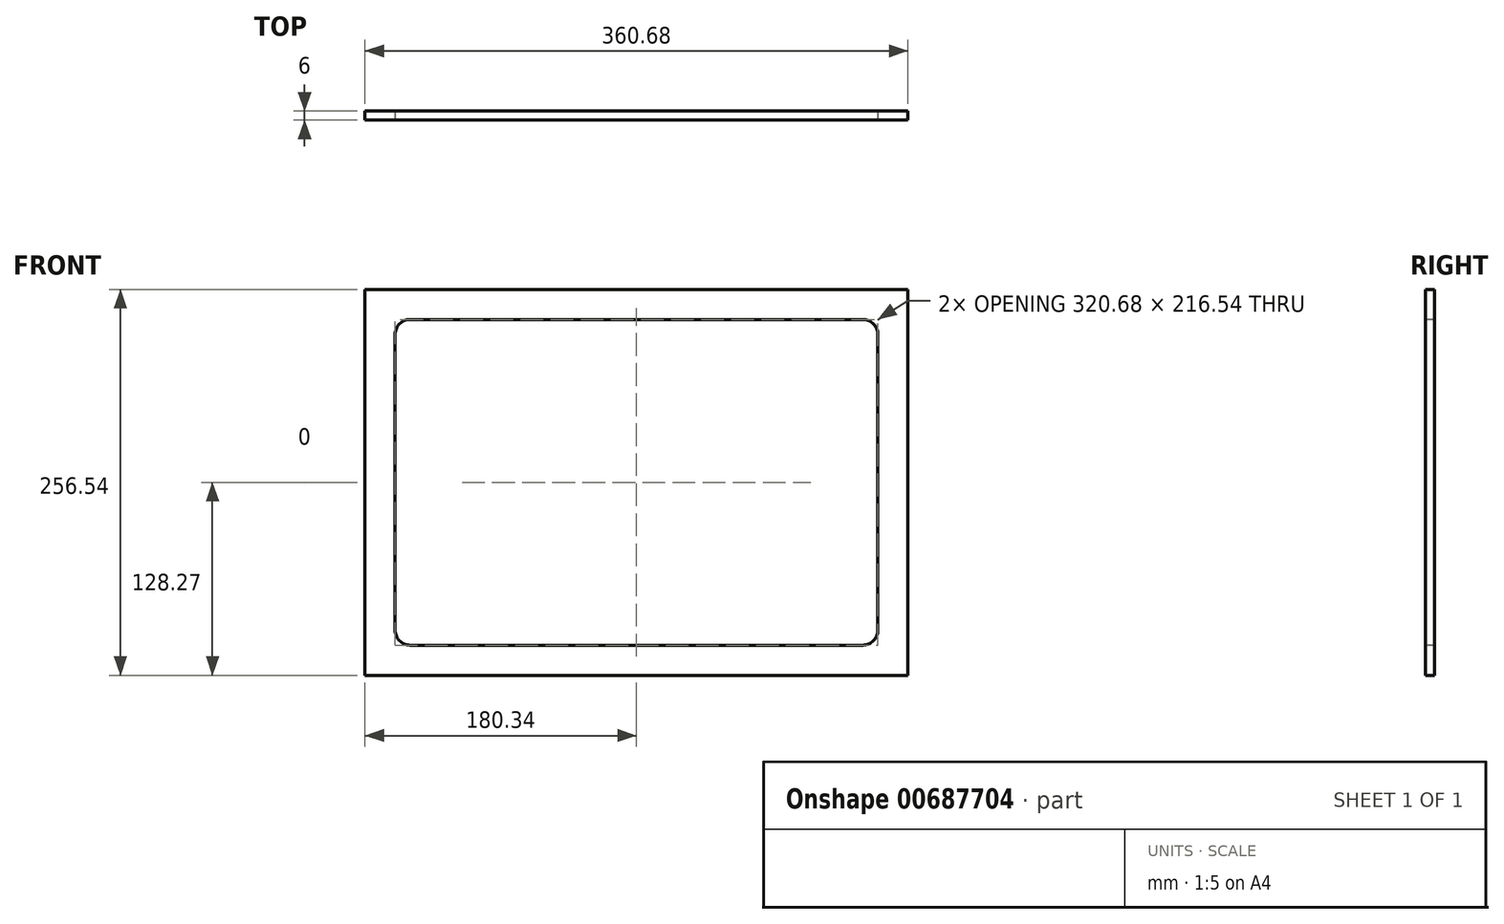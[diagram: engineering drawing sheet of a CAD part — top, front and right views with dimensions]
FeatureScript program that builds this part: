
annotation { "Feature Type Name" : "Feature", "Feature Type Description" : "" }
export const myFeature = defineFeature(function(context is Context, id is Id, definition is map)
    precondition{}
    {
        {
            var Q0;
            Q0=qCreatedBy(makeId("Front.planeOp"),FACE);
            var sketch = newSketch(context, id + "F0", { "sketchPlane" : qUnion([Q0])});
            skLineSegment(sketch, "E0.bottom", {"start": v(-180.34, 128.27) * mm, "end": v(180.34, 128.27) * mm});
            skLineSegment(sketch, "E0.top", {"start": v(-180.34, -128.27) * mm, "end": v(180.34, -128.27) * mm});
            skLineSegment(sketch, "E0.left", {"start": v(-180.34, 128.27) * mm, "end": v(-180.34, -128.27) * mm});
            skLineSegment(sketch, "E0.right", {"start": v(180.34, 128.27) * mm, "end": v(180.34, -128.27) * mm});
            skLineSegment(sketch, "E1", {"start": v(0, 0) * mm, "end": v(0, 128.27) * mm, "construction": true});
            skLineSegment(sketch, "E2", {"start": v(0, 0) * mm, "end": v(0, -128.27) * mm, "construction": true});
            skLineSegment(sketch, "E3", {"start": v(0, 0) * mm, "end": v(-180.34, 0) * mm, "construction": true});
            skLineSegment(sketch, "E4", {"start": v(0, 0) * mm, "end": v(180.34, 0) * mm, "construction": true});
            skLineSegment(sketch, "E5.0", {"start": v(-150.34, 108.27) * mm, "end": v(150.34, 108.27) * mm});
            skLineSegment(sketch, "E5.1", {"start": v(-160.34, 98.27) * mm, "end": v(-160.34, -98.27) * mm});
            skLineSegment(sketch, "E5.2", {"start": v(-150.34, -108.27) * mm, "end": v(150.34, -108.27) * mm});
            skLineSegment(sketch, "E5.3", {"start": v(160.34, 98.27) * mm, "end": v(160.34, -98.27) * mm});
            skPoint(sketch, "E6.visualSharp", {"position": v(-160.34, 108.27) * mm});
            skArc(sketch, "E6.filletArc", {"start": v(-150.34, 108.27) * mm, "mid": v(-157.41, 105.34) * mm, "end": v(-160.34, 98.27) * mm});
            skPoint(sketch, "E7.visualSharp", {"position": v(160.34, 108.27) * mm});
            skArc(sketch, "E7.filletArc", {"start": v(160.34, 98.27) * mm, "mid": v(157.41, 105.34) * mm, "end": v(150.34, 108.27) * mm});
            skPoint(sketch, "E8.visualSharp", {"position": v(160.34, -108.27) * mm});
            skArc(sketch, "E8.filletArc", {"start": v(150.34, -108.27) * mm, "mid": v(157.41, -105.34) * mm, "end": v(160.34, -98.27) * mm});
            skPoint(sketch, "E9.visualSharp", {"position": v(-160.34, -108.27) * mm});
            skArc(sketch, "E9.filletArc", {"start": v(-160.34, -98.27) * mm, "mid": v(-157.41, -105.34) * mm, "end": v(-150.34, -108.27) * mm});
            skSolve(sketch);
        }
        {
            var Q0;
            Q0=qSketchRegion(id+"F0",true);
            extrude(context, id + "F1", {"entities" : qUnion([Q0]), "oppositeDirection" : true, "depth" : 6 * mm, "offsetDistance" : 25 * mm});
        }
        {
            var Q0;
            Q0=qCreatedBy(makeId("Front.planeOp"),FACE);
            cPlane(context, id + "F2", {"entities" : qUnion([Q0]), "cplaneType" : CPlaneType.OFFSET, "offset" : 139.7 * mm, "oppositeDirection" : true, "width" : 150 * mm, "height" : 150 * mm});
        }
    });
